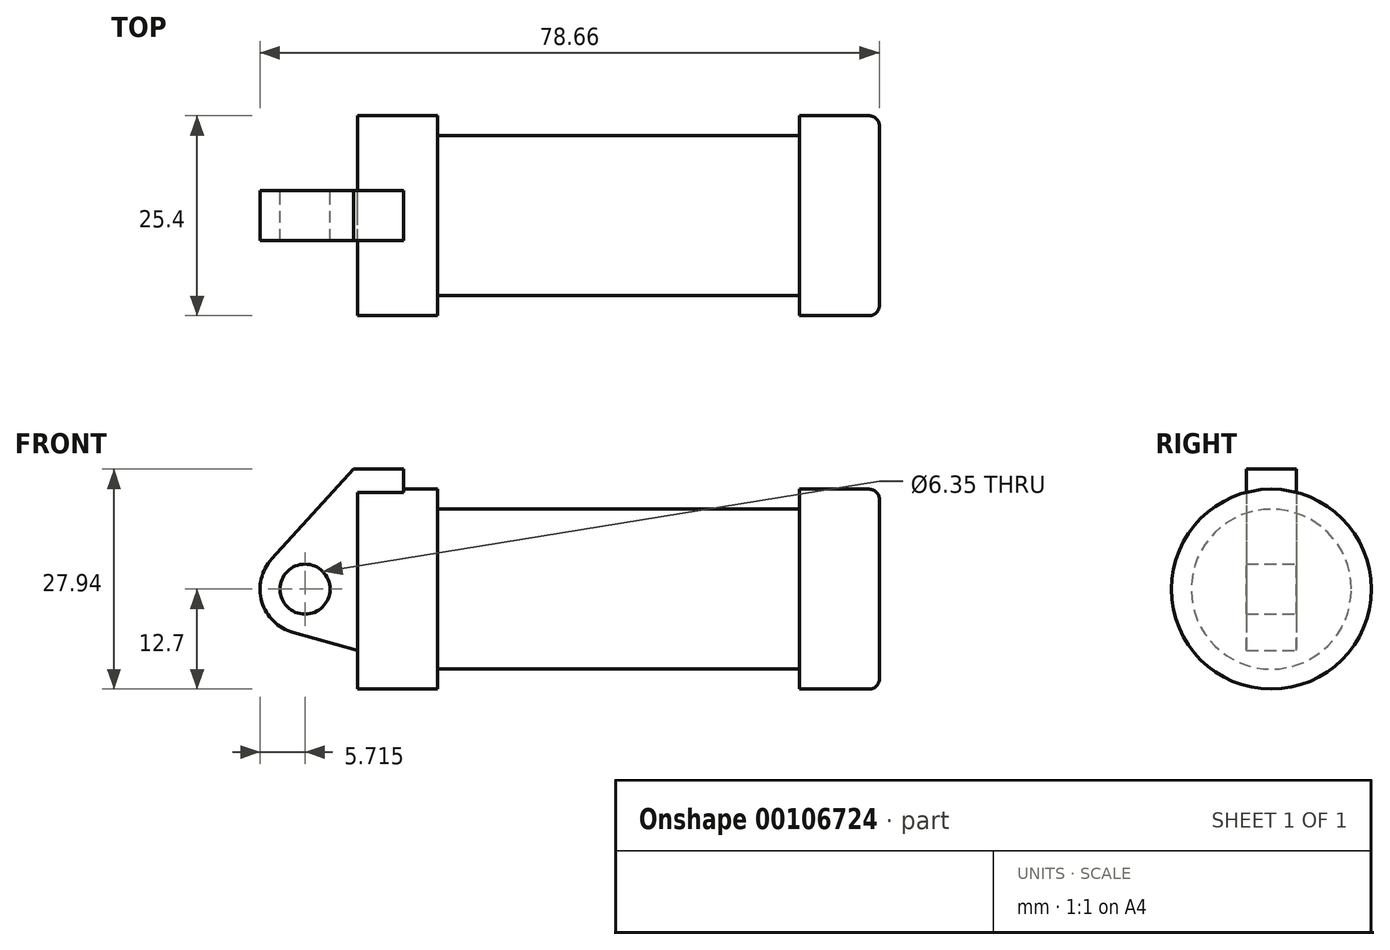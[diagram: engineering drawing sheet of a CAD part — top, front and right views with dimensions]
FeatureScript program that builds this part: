
annotation { "Feature Type Name" : "Feature", "Feature Type Description" : "" }
export const myFeature = defineFeature(function(context is Context, id is Id, definition is map)
    precondition{}
    {
        {
            var Q0;
            Q0=qCreatedBy(makeId("Front.planeOp"),FACE);
            var sketch = newSketch(context, id + "F0", { "sketchPlane" : qUnion([Q0])});
            skLineSegment(sketch, "E0", {"start": v(0, 0) * mm, "end": v(0, 12.7) * mm});
            skLineSegment(sketch, "E1", {"start": v(0, 12.7) * mm, "end": v(10.16, 12.7) * mm});
            skLineSegment(sketch, "E2", {"start": v(10.16, 12.7) * mm, "end": v(10.16, 10.16) * mm});
            skLineSegment(sketch, "E3", {"start": v(10.16, 10.16) * mm, "end": v(56.13, 10.16) * mm});
            skLineSegment(sketch, "E4", {"start": v(56.13, 10.16) * mm, "end": v(56.13, 12.7) * mm});
            skLineSegment(sketch, "E5", {"start": v(56.13, 12.7) * mm, "end": v(66.3, 12.7) * mm});
            skLineSegment(sketch, "E6", {"start": v(66.3, 12.7) * mm, "end": v(66.3, 0) * mm});
            skLineSegment(sketch, "E7", {"start": v(66.3, 0) * mm, "end": v(0, 0) * mm});
            skLineSegment(sketch, "E8", {"start": v(5.84, 15.24) * mm, "end": v(-0.5, 15.24) * mm});
            skLineSegment(sketch, "E9", {"start": v(-0.5, 15.24) * mm, "end": v(-10.88, 3.85) * mm});
            skLineSegment(sketch, "E10", {"start": v(0, 0) * mm, "end": v(-6.65, 0) * mm});
            skCircle(sketch, "E11", {"center": v(-6.65, 0) * mm, "radius": 5.72 * mm});
            skCircle(sketch, "E12", {"center": v(-6.65, 0) * mm, "radius": 3.18 * mm});
            skLineSegment(sketch, "E13", {"start": v(5.84, 15.24) * mm, "end": v(5.84, -9.4) * mm});
            skLineSegment(sketch, "E14", {"start": v(5.84, -9.4) * mm, "end": v(-8.18, -5.5) * mm});
            skSolve(sketch);
        }
        {
            var Q0;
            {var subQ0=sQuery(id+"F0.wireOp",EDGE,"E0");Q0=makeQuery(id+"F0.imprint","IMPRINT",FACE,{"disambiguationData":[TD([[makeQuery(id+"F0.imprint","IMPRINT",EDGE,{"derivedFrom":subQ0}),-1.0]])]});}
            var Q1;
            {var subQ0=sQuery(id+"F0.wireOp",EDGE,"E2");Q1=makeQuery(id+"F0.imprint","IMPRINT",FACE,{"disambiguationData":[TD([[makeQuery(id+"F0.imprint","IMPRINT",EDGE,{"derivedFrom":subQ0}),-1.0]])]});}
            var Q2;
            Q2=sQuery(id+"F0.wireOp",EDGE,"E7");
            revolve(context, id + "F1", {"entities" : qUnion([Q0, Q1]), "axis" : qUnion([Q2]), "revolveType" : RevolveType.FULL});
        }
        {
            var Q0;
            {var subQ3=sQuery(id+"F0.wireOp",EDGE,"E0");Q0=makeQuery(id+"F0.imprint","IMPRINT",FACE,{"disambiguationData":[TD([[makeQuery(id+"F0.imprint","IMPRINT",EDGE,{"derivedFrom":subQ3}),1.0]])]});}
            var Q1;
            {var subQ4=sQuery(id+"F0.wireOp",EDGE,"E12");Q1=makeQuery(id+"F0.imprint","IMPRINT",FACE,{"disambiguationData":[TD([[makeQuery(id+"F0.imprint","IMPRINT",EDGE,{"derivedFrom":subQ4}),-1.0]])]});}
            var Q2;
            {var subQ0=sQuery(id+"F0.wireOp",EDGE,"E14");Q2=makeQuery(id+"F0.imprint","IMPRINT",FACE,{"disambiguationData":[TD([[makeQuery(id+"F0.imprint","IMPRINT",EDGE,{"derivedFrom":subQ0}),-1.0]])]});}
            var Q3;
            {var subQ0=sQuery(id+"F0.wireOp",EDGE,"E0");Q3=makeQuery(id+"F0.imprint","IMPRINT",FACE,{"disambiguationData":[TD([[makeQuery(id+"F0.imprint","IMPRINT",EDGE,{"derivedFrom":subQ0}),-1.0]])]});}
            extrude(context, id + "F2", {"entities" : qUnion([Q0, Q1, Q2, Q3]), "operationType" : NewBodyOperationType.ADD, "endBound" : BoundingType.SYMMETRIC, "depth" : 6.35 * mm});
        }
        {
            var Q0;
            Q0=makeQuery(id+"F1.opRevolve","SWEPT_EDGE",EDGE,{"disambiguationData":[OSD([sQuery(id+"F0.wireOp",EDGE,"E5"),sQuery(id+"F0.wireOp",EDGE,"E6")])]});
            fillet(context, id + "F3", {"entities" : qUnion([Q0]), "radius" : 1.27 * mm, "tangentPropagation" : true, "allowEdgeOverflow" : false});
        }
    });
